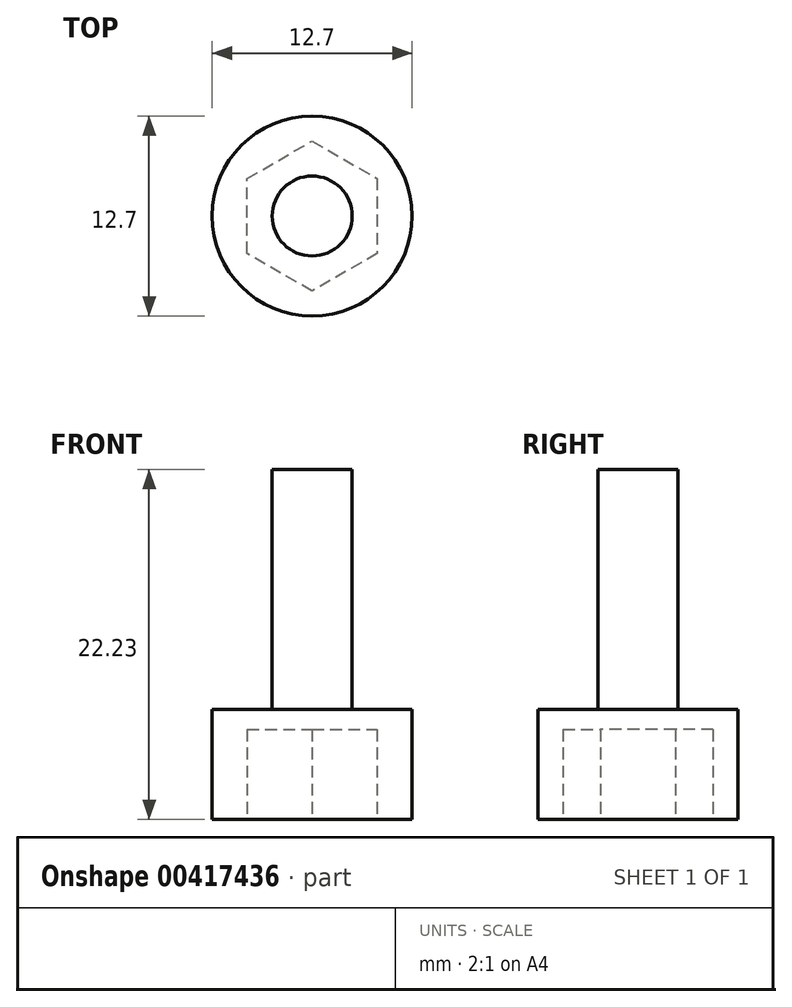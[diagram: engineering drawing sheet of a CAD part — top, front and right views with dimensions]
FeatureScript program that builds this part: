
annotation { "Feature Type Name" : "Feature", "Feature Type Description" : "" }
export const myFeature = defineFeature(function(context is Context, id is Id, definition is map)
    precondition{}
    {
        {
            var Q0;
            Q0=qCreatedBy(makeId("Top.planeOp"),FACE);
            var sketch = newSketch(context, id + "F0", { "sketchPlane" : qUnion([Q0])});
            skCircle(sketch, "E0", {"center": v(0, 0) * mm, "radius": 6.35 * mm});
            skCircle(sketch, "E1", {"center": v(0, 0) * mm, "radius": 2.54 * mm});
            skCircle(sketch, "E2.cCircle", {"center": v(0, 0) * mm, "radius": 4.13 * mm, "construction": true});
            skLineSegment(sketch, "E2.0", {"start": v(4.13, 2.38) * mm, "end": v(4.13, -2.38) * mm});
            skLineSegment(sketch, "E2.1", {"start": v(4.13, -2.38) * mm, "end": v(0, -4.77) * mm});
            skLineSegment(sketch, "E2.2", {"start": v(0, -4.77) * mm, "end": v(-4.13, -2.38) * mm});
            skLineSegment(sketch, "E2.3", {"start": v(-4.13, -2.38) * mm, "end": v(-4.13, 2.38) * mm});
            skLineSegment(sketch, "E2.4", {"start": v(-4.13, 2.38) * mm, "end": v(0, 4.77) * mm});
            skLineSegment(sketch, "E2.5", {"start": v(0, 4.77) * mm, "end": v(4.13, 2.38) * mm});
            skPoint(sketch, "E2.0.midPoint", {"position": v(4.13, 0) * mm});
            skSolve(sketch);
        }
        {
            var Q0;
            Q0=makeQuery(id+"F0.imprint","IMPRINT",FACE,{"disambiguationData":[TD([[makeQuery(id+"F0.imprint","IMPRINT",EDGE,{"derivedFrom":sQuery(id+"F0.wireOp",EDGE,"E0")}),1.0]])]});
            var Q1;
            Q1=makeQuery(id+"F0.imprint","IMPRINT",FACE,{"disambiguationData":[TD([[makeQuery(id+"F0.imprint","IMPRINT",EDGE,{"derivedFrom":sQuery(id+"F0.wireOp",EDGE,"E1")}),-1.0]])]});
            extrude(context, id + "F1", {"entities" : qUnion([Q0, Q1]), "depth" : 7 * mm});
        }
        {
            var Q0;
            Q0=makeQuery(id+"F0.imprint","IMPRINT",FACE,{"disambiguationData":[TD([[makeQuery(id+"F0.imprint","IMPRINT",EDGE,{"derivedFrom":sQuery(id+"F0.wireOp",EDGE,"E1")}),1.0]])]});
            extrude(context, id + "F2", {"entities" : qUnion([Q0]), "operationType" : NewBodyOperationType.ADD, "depth" : 22.22 * mm});
        }
        {
            var Q0;
            Q0=makeQuery(id+"F0.imprint","IMPRINT",FACE,{"disambiguationData":[TD([[makeQuery(id+"F0.imprint","IMPRINT",EDGE,{"derivedFrom":sQuery(id+"F0.wireOp",EDGE,"E1")}),-1.0]])]});
            var Q1;
            Q1=makeQuery(id+"F0.imprint","IMPRINT",FACE,{"disambiguationData":[TD([[makeQuery(id+"F0.imprint","IMPRINT",EDGE,{"derivedFrom":sQuery(id+"F0.wireOp",EDGE,"E1")}),1.0]])]});
            extrude(context, id + "F3", {"entities" : qUnion([Q0, Q1]), "operationType" : NewBodyOperationType.REMOVE, "depth" : 5.7 * mm});
        }
    });
